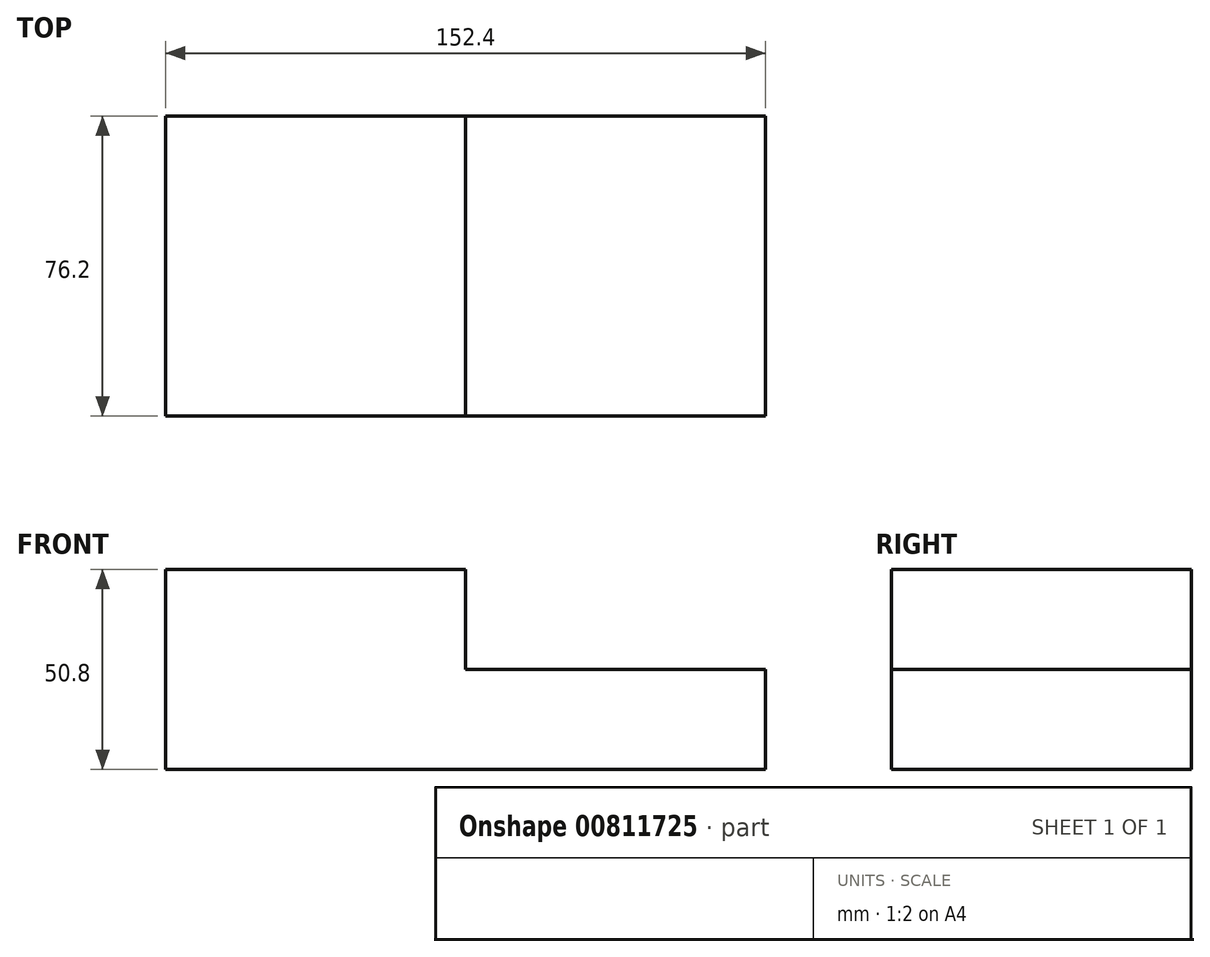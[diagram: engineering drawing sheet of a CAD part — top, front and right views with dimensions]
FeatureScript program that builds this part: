
annotation { "Feature Type Name" : "Feature", "Feature Type Description" : "" }
export const myFeature = defineFeature(function(context is Context, id is Id, definition is map)
    precondition{}
    {
        {
            var Q0;
            Q0=qCreatedBy(makeId("Front.planeOp"),FACE);
            var sketch = newSketch(context, id + "F0", { "sketchPlane" : qUnion([Q0])});
            skLineSegment(sketch, "E0", {"start": v(-68.62, 0) * mm, "end": v(-68.62, 50.8) * mm});
            skLineSegment(sketch, "E1", {"start": v(-68.62, 50.8) * mm, "end": v(7.58, 50.8) * mm});
            skLineSegment(sketch, "E2", {"start": v(7.58, 50.8) * mm, "end": v(7.58, 25.4) * mm});
            skLineSegment(sketch, "E3", {"start": v(7.58, 25.4) * mm, "end": v(83.78, 25.4) * mm});
            skLineSegment(sketch, "E4", {"start": v(83.78, 25.4) * mm, "end": v(83.78, 0) * mm});
            skLineSegment(sketch, "E5", {"start": v(-68.62, 0) * mm, "end": v(83.78, 0) * mm});
            skSolve(sketch);
        }
        {
            var Q0;
            Q0=makeQuery(id+"F0.imprint","IMPRINT",FACE,{"disambiguationData":[TD([[makeQuery(id+"F0.imprint","IMPRINT",EDGE,{"derivedFrom":sQuery(id+"F0.wireOp",EDGE,"E0")}),-1.0]])]});
            extrude(context, id + "F1", {"entities" : qUnion([Q0]), "depth" : 76.2 * mm, "offsetDistance" : 25.4 * mm});
        }
    });
